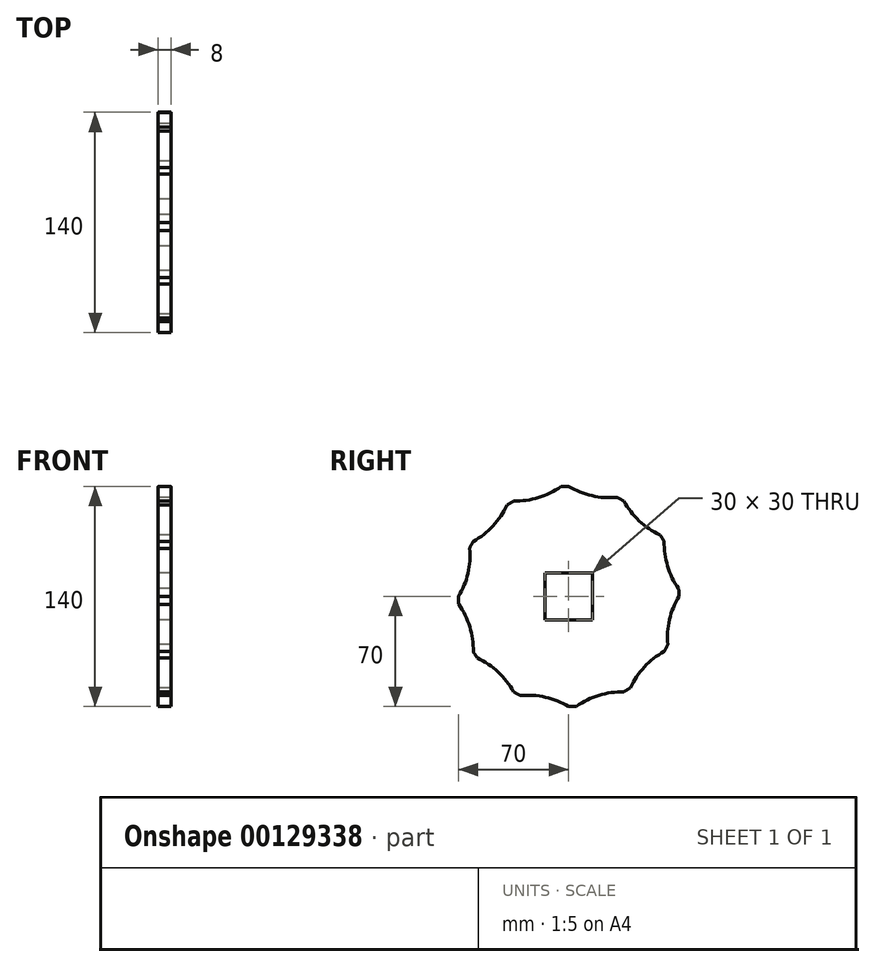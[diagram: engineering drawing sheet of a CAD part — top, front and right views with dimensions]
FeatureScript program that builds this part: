
annotation { "Feature Type Name" : "Feature", "Feature Type Description" : "" }
export const myFeature = defineFeature(function(context is Context, id is Id, definition is map)
    precondition{}
    {
        {
            var Q0;
            Q0=qCreatedBy(makeId("Right.planeOp"),FACE);
            var sketch = newSketch(context, id + "F0", { "sketchPlane" : qUnion([Q0])});
            skLineSegment(sketch, "E0.bottom", {"start": v(-15, -15) * mm, "end": v(15, -15) * mm});
            skLineSegment(sketch, "E0.top", {"start": v(-15, 15) * mm, "end": v(15, 15) * mm});
            skLineSegment(sketch, "E0.left", {"start": v(-15, -15) * mm, "end": v(-15, 15) * mm});
            skLineSegment(sketch, "E0.right", {"start": v(15, -15) * mm, "end": v(15, 15) * mm});
            skPoint(sketch, "E0.middle", {"position": v(0, 0) * mm});
            skArc(sketch, "E1", {"start": v(-60.62, 35) * mm, "mid": v(-61.82, 32.84) * mm, "end": v(-62.94, 30.63) * mm});
            skLineSegment(sketch, "E2", {"start": v(0, 0) * mm, "end": v(0, 62.26) * mm});
            skArc(sketch, "E3", {"start": v(0, 70) * mm, "mid": v(14.75, 64) * mm, "end": v(30.63, 62.94) * mm});
            skArc(sketch, "E4.1.0", {"start": v(-60.62, -35) * mm, "mid": v(-62.8, -19.23) * mm, "end": v(-69.83, -4.95) * mm});
            skArc(sketch, "E4.2.0", {"start": v(60.62, -35) * mm, "mid": v(48.05, -44.77) * mm, "end": v(39.2, -58) * mm});
            skArc(sketch, "E5.1.0", {"start": v(-35, 60.62) * mm, "mid": v(-19.23, 62.8) * mm, "end": v(-4.95, 69.83) * mm});
            skArc(sketch, "E5.2.0", {"start": v(-60.62, 35) * mm, "mid": v(-48.05, 44.77) * mm, "end": v(-39.2, 58) * mm});
            skArc(sketch, "E5.3.0", {"start": v(-70, 0) * mm, "mid": v(-64, 14.75) * mm, "end": v(-62.94, 30.63) * mm});
            skArc(sketch, "E5.5.0", {"start": v(-35, -60.62) * mm, "mid": v(-44.77, -48.05) * mm, "end": v(-58, -39.2) * mm});
            skArc(sketch, "E5.6.0", {"start": v(0, -70) * mm, "mid": v(-14.75, -64) * mm, "end": v(-30.63, -62.94) * mm});
            skArc(sketch, "E5.7.0", {"start": v(35, -60.62) * mm, "mid": v(19.23, -62.8) * mm, "end": v(4.95, -69.83) * mm});
            skArc(sketch, "E5.9.0", {"start": v(70, 0) * mm, "mid": v(64, -14.75) * mm, "end": v(62.94, -30.63) * mm});
            skArc(sketch, "E5.10.0", {"start": v(60.62, 35) * mm, "mid": v(62.8, 19.23) * mm, "end": v(69.83, 4.95) * mm});
            skArc(sketch, "E5.11.0", {"start": v(35, 60.62) * mm, "mid": v(44.77, 48.05) * mm, "end": v(58, 39.2) * mm});
            skArc(sketch, "E6.trimOffspring", {"start": v(-35, 60.62) * mm, "mid": v(-37.12, 59.35) * mm, "end": v(-39.2, 58) * mm});
            skArc(sketch, "E7.trimOffspring", {"start": v(0, 70) * mm, "mid": v(-2.47, 69.96) * mm, "end": v(-4.95, 69.83) * mm});
            skArc(sketch, "E8.trimOffspring", {"start": v(35, 60.62) * mm, "mid": v(32.84, 61.82) * mm, "end": v(30.63, 62.94) * mm});
            skArc(sketch, "E9.trimOffspring", {"start": v(60.62, 35) * mm, "mid": v(59.35, 37.12) * mm, "end": v(58, 39.2) * mm});
            skArc(sketch, "E10.trimOffspring", {"start": v(70, 0) * mm, "mid": v(69.96, 2.47) * mm, "end": v(69.83, 4.95) * mm});
            skArc(sketch, "E11.trimOffspring", {"start": v(60.62, -35) * mm, "mid": v(61.82, -32.84) * mm, "end": v(62.94, -30.63) * mm});
            skArc(sketch, "E12.trimOffspring", {"start": v(35, -60.62) * mm, "mid": v(37.12, -59.35) * mm, "end": v(39.2, -58) * mm});
            skArc(sketch, "E13.trimOffspring", {"start": v(0, -70) * mm, "mid": v(2.47, -69.96) * mm, "end": v(4.95, -69.83) * mm});
            skArc(sketch, "E14.trimOffspring", {"start": v(-35, -60.62) * mm, "mid": v(-32.84, -61.82) * mm, "end": v(-30.63, -62.94) * mm});
            skArc(sketch, "E15.trimOffspring", {"start": v(-60.62, -35) * mm, "mid": v(-59.35, -37.12) * mm, "end": v(-58, -39.2) * mm});
            skArc(sketch, "E16.trimOffspring", {"start": v(-70, 0) * mm, "mid": v(-69.96, -2.47) * mm, "end": v(-69.83, -4.95) * mm});
            skSolve(sketch);
        }
        {
            var Q0;
            Q0=makeQuery(id+"F0.imprint","IMPRINT",FACE,{"disambiguationData":[TD([[makeQuery(id+"F0.imprint","IMPRINT",EDGE,{"derivedFrom":sQuery(id+"F0.wireOp",EDGE,"E0.bottom")}),-1.0]])]});
            extrude(context, id + "F1", {"entities" : qUnion([Q0]), "depth" : 8 * mm});
        }
    });
